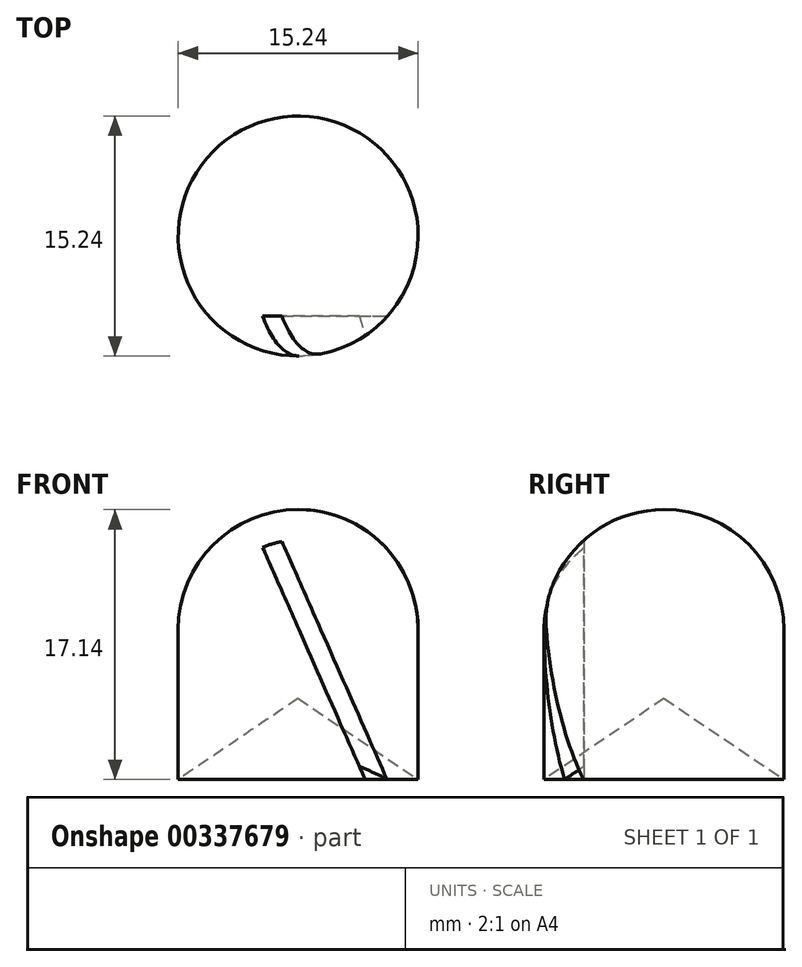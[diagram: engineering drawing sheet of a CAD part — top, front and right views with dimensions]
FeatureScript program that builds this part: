
annotation { "Feature Type Name" : "Feature", "Feature Type Description" : "" }
export const myFeature = defineFeature(function(context is Context, id is Id, definition is map)
    precondition{}
    {
        {
            var Q0;
            Q0=qCreatedBy(makeId("Front.planeOp"),FACE);
            var sketch = newSketch(context, id + "F0", { "sketchPlane" : qUnion([Q0])});
            skLineSegment(sketch, "E0", {"start": v(-7.62, -5.14) * mm, "end": v(-7.62, 4.38) * mm});
            skArc(sketch, "E1", {"start": v(-7.62, 4.38) * mm, "mid": v(-5.39, 9.77) * mm, "end": v(0, 12) * mm});
            skLineSegment(sketch, "E2", {"start": v(0, 12) * mm, "end": v(0, -5.14) * mm});
            skLineSegment(sketch, "E3", {"start": v(0, -5.14) * mm, "end": v(-7.62, -5.14) * mm});
            skLineSegment(sketch, "E4", {"start": v(0, 21.2) * mm, "end": v(0, -17.88) * mm});
            skSolve(sketch);
        }
        {
            var Q0;
            Q0=makeQuery(id+"F0.imprint","IMPRINT",FACE,{"disambiguationData":[TD([[makeQuery(id+"F0.imprint","IMPRINT",EDGE,{"derivedFrom":sQuery(id+"F0.wireOp",EDGE,"E0")}),-1.0]])]});
            var Q1;
            Q1=sQuery(id+"F0.wireOp",EDGE,"E2");
            revolve(context, id + "F1", {"entities" : qUnion([Q0]), "axis" : qUnion([Q1]), "revolveType" : RevolveType.FULL});
        }
        {
            var Q1;
            Q1=makeQuery(id+"F1.opRevolve","SWEPT_FACE",FACE,{"disambiguationData":[OSD([sQuery(id+"F0.wireOp",EDGE,"E3")])]});
            var Q2;
            Q2=qCreatedBy(makeId("Origin.pointOp"),VERTEX);
            loft(context, id + "F2", {"operationType" : NewBodyOperationType.REMOVE, "sheetProfilesArray" : [{ "sheetProfileEntities" : qUnion([Q1]) }, { "sheetProfileEntities" : qUnion([Q2]) }]});
        }
        {
            var Q0;
            Q0=qCreatedBy(makeId("Front.planeOp"),FACE);
            cPlane(context, id + "F3", {"entities" : qUnion([Q0]), "cplaneType" : CPlaneType.OFFSET, "offset" : 5.08 * mm, "width" : 152.4 * mm, "height" : 152.4 * mm});
        }
        {
            var Q0;
            Q0=qCreatedBy(id+"F3.planeOp",FACE);
            var sketch = newSketch(context, id + "F4", { "sketchPlane" : qUnion([Q0])});
            skLineSegment(sketch, "E5", {"start": v(7.88, -10.22) * mm, "end": v(6.72, -10.74) * mm});
            skLineSegment(sketch, "E6", {"start": v(6.72, -10.74) * mm, "end": v(-12.29, 32.3) * mm});
            skLineSegment(sketch, "E7", {"start": v(-12.29, 32.3) * mm, "end": v(-11.13, 32.82) * mm});
            skLineSegment(sketch, "E8", {"start": v(-11.13, 32.82) * mm, "end": v(7.88, -10.22) * mm});
            skSolve(sketch);
        }
        {
            var Q0;
            Q0 = qSketchRegion(id + "F4", true);
            extrude(context, id + "F5", {"entities" : qUnion([Q0]), "operationType" : NewBodyOperationType.REMOVE, "flatOperationType" : FlatOperationType.REMOVE, "offsetDistance" : 25.4 * mm, "depth" : 25.4 * mm, "domain" : OperationDomain.MODEL});
        }
    });
